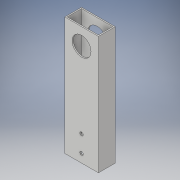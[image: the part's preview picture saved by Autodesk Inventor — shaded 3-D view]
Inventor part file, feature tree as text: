
AUTODESK INVENTOR PART (.ipt)
format: ipt  version: 2018 (Build 220112000, 112)  size: 125,952 bytes
history: native  units: in
note: dims shown in document units (in); Inventor stores cm internally (conversion verified against a paired STEP export)
features: extrude x3, sketch x3
ambient origin geometry x8: Origin, YZ Plane, XZ Plane, XY Plane, X Axis, Y Axis, Z Axis, Center Point
bodies: Solid1 (feature_tree)
feature tree (6):
  extrude  "Extrusion1"  Depth=7.0in
  extrude  "Extrusion2"  Depth=0.075in
  extrude  "Extrusion3"  Depth=1.0in
  sketch  "Sketch1"  dims[d0=2.0in d1=7.0in]
  sketch  "Sketch2"  dims[d2=1.0in d3=0.0in d4=0.075in]
  sketch  "Sketch3"  dims[d5=20.0in d6=0.0in d7=0.5in d8=1.0in d9=1.0in d10=1.1225in d11=0.2031in d12=0.2031in d13=20.0in d14=0.0in]
